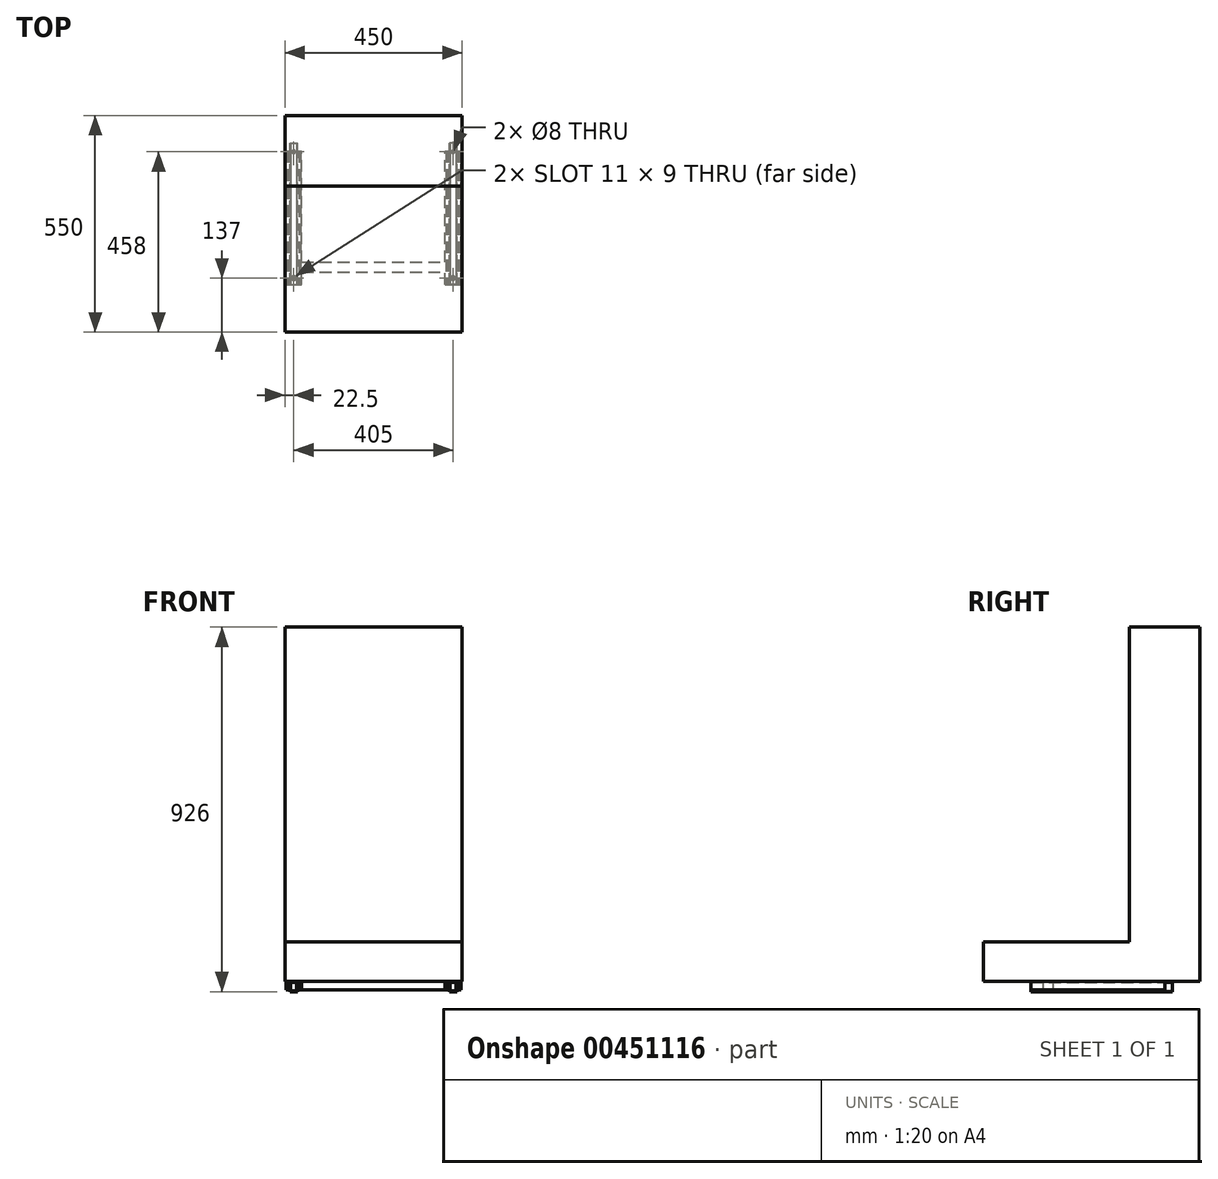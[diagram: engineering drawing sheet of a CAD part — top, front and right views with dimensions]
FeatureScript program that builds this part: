
annotation { "Feature Type Name" : "Feature", "Feature Type Description" : "" }
export const myFeature = defineFeature(function(context is Context, id is Id, definition is map)
    precondition{}
    {
        {
            var Q0;
            Q0=qCreatedBy(makeId("Right.planeOp"),FACE);
            var sketch = newSketch(context, id + "F0", { "sketchPlane" : qUnion([Q0])});
            skLineSegment(sketch, "E0.bottom", {"start": v(0, 0) * mm, "end": v(-550, 0) * mm});
            skLineSegment(sketch, "E0.top", {"start": v(0, 100) * mm, "end": v(-550, 100) * mm});
            skLineSegment(sketch, "E0.left", {"start": v(0, 0) * mm, "end": v(0, 100) * mm});
            skLineSegment(sketch, "E0.right", {"start": v(-550, 0) * mm, "end": v(-550, 100) * mm});
            skLineSegment(sketch, "E1.bottom", {"start": v(0, 100) * mm, "end": v(-179.87, 100) * mm});
            skLineSegment(sketch, "E1.top", {"start": v(0, 900) * mm, "end": v(-179.87, 900) * mm});
            skLineSegment(sketch, "E1.left", {"start": v(0, 100) * mm, "end": v(0, 900) * mm});
            skLineSegment(sketch, "E1.right", {"start": v(-179.87, 100) * mm, "end": v(-179.87, 900) * mm});
            skSolve(sketch);
        }
        {
            var Q0;
            Q0 = qSketchRegion(id + "F0", true);
            extrude(context, id + "F1", {"entities" : qUnion([Q0]), "depth" : 450 * mm, "offsetDistance" : 25 * mm});
        }
        {
            var Q0;
            Q0=makeQuery(id+"F1.opExtrude","SWEPT_FACE",FACE,{"disambiguationData":[OSD([sQuery(id+"F0.wireOp",EDGE,"E0.bottom")])]});
            var sketch = newSketch(context, id + "F2", { "sketchPlane" : qUnion([Q0])});
            skLineSegment(sketch, "E2.bottom", {"start": v(2.5, 430) * mm, "end": v(42.5, 430) * mm});
            skLineSegment(sketch, "E2.top", {"start": v(2.5, 90) * mm, "end": v(42.5, 90) * mm});
            skLineSegment(sketch, "E2.left", {"start": v(2.5, 430) * mm, "end": v(2.5, 90) * mm});
            skLineSegment(sketch, "E2.right", {"start": v(42.5, 430) * mm, "end": v(42.5, 90) * mm});
            skLineSegment(sketch, "E3.bottom", {"start": v(407.5, 430) * mm, "end": v(447.5, 430) * mm});
            skLineSegment(sketch, "E3.top", {"start": v(407.5, 90) * mm, "end": v(447.5, 90) * mm});
            skLineSegment(sketch, "E3.left", {"start": v(407.5, 430) * mm, "end": v(407.5, 90) * mm});
            skLineSegment(sketch, "E3.right", {"start": v(447.5, 430) * mm, "end": v(447.5, 90) * mm});
            skLineSegment(sketch, "E4.bottom", {"start": v(42.5, 397.78) * mm, "end": v(407.5, 397.78) * mm});
            skLineSegment(sketch, "E4.top", {"start": v(42.5, 372.84) * mm, "end": v(407.5, 372.84) * mm});
            skLineSegment(sketch, "E4.left", {"start": v(42.5, 397.78) * mm, "end": v(42.5, 372.84) * mm});
            skLineSegment(sketch, "E4.right", {"start": v(407.5, 397.78) * mm, "end": v(407.5, 372.84) * mm});
            skSolve(sketch);
        }
        {
            var Q0;
            Q0 = qSketchRegion(id + "F2", true);
            extrude(context, id + "F3", {"entities" : qUnion([Q0]), "depth" : 22 * mm, "offsetDistance" : 25 * mm});
        }
        {
            var Q0;
            Q0=makeQuery(id+"F3.opExtrude","SWEPT_FACE",FACE,{"disambiguationData":[OSD([sQuery(id+"F2.wireOp",EDGE,"E2.bottom")])]});
            var sketch = newSketch(context, id + "F4", { "sketchPlane" : qUnion([Q0])});
            skLineSegment(sketch, "E5.bottom", {"start": v(4.5, -2) * mm, "end": v(40.5, -2) * mm});
            skLineSegment(sketch, "E5.top", {"start": v(4.5, -20) * mm, "end": v(40.5, -20) * mm});
            skLineSegment(sketch, "E5.left", {"start": v(4.5, -2) * mm, "end": v(4.5, -20) * mm});
            skLineSegment(sketch, "E5.right", {"start": v(40.5, -2) * mm, "end": v(40.5, -20) * mm});
            skLineSegment(sketch, "E6.bottom", {"start": v(9.5, -20) * mm, "end": v(35.5, -20) * mm});
            skLineSegment(sketch, "E6.top", {"start": v(9.5, -22) * mm, "end": v(35.5, -22) * mm});
            skLineSegment(sketch, "E6.left", {"start": v(9.5, -20) * mm, "end": v(9.5, -22) * mm});
            skLineSegment(sketch, "E6.right", {"start": v(35.5, -20) * mm, "end": v(35.5, -22) * mm});
            skLineSegment(sketch, "E7.0", {"start": v(407.5, -22) * mm, "end": v(407.5, 0) * mm});
            skLineSegment(sketch, "E8.0", {"start": v(407.5, -22) * mm, "end": v(447.5, -22) * mm});
            skLineSegment(sketch, "E9.0", {"start": v(447.5, -22) * mm, "end": v(447.5, 0) * mm});
            skLineSegment(sketch, "E10.bottom", {"start": v(409.5, -2) * mm, "end": v(445.5, -2) * mm});
            skLineSegment(sketch, "E10.top", {"start": v(409.5, -20) * mm, "end": v(445.5, -20) * mm});
            skLineSegment(sketch, "E10.left", {"start": v(409.5, -2) * mm, "end": v(409.5, -20) * mm});
            skLineSegment(sketch, "E10.right", {"start": v(445.5, -2) * mm, "end": v(445.5, -20) * mm});
            skLineSegment(sketch, "E11.bottom", {"start": v(414.5, -20) * mm, "end": v(440.5, -20) * mm});
            skLineSegment(sketch, "E11.top", {"start": v(414.5, -22) * mm, "end": v(440.5, -22) * mm});
            skLineSegment(sketch, "E11.left", {"start": v(414.5, -20) * mm, "end": v(414.5, -22) * mm});
            skLineSegment(sketch, "E11.right", {"start": v(440.5, -20) * mm, "end": v(440.5, -22) * mm});
            skSolve(sketch);
        }
        {
            var Q0;
            Q0 = qSketchRegion(id + "F4", true);
            extrude(context, id + "F5", {"entities" : qUnion([Q0]), "operationType" : NewBodyOperationType.REMOVE, "oppositeDirection" : true, "depth" : 372 * mm, "offsetDistance" : 25 * mm});
        }
        {
            var Q0;
            Q0=makeQuery(id+"F5.boolean.opBoolean","COPY",FACE,{"derivedFrom":makeQuery(id+"F5.opExtrude","SWEPT_FACE",FACE,{"disambiguationData":[OSD([sQuery(id+"F4.wireOp",EDGE,"E5.bottom")])]})});
            var sketch = newSketch(context, id + "F6", { "sketchPlane" : qUnion([Q0])});
            skLineSegment(sketch, "E12.bottom", {"start": v(13, 430) * mm, "end": v(32, 430) * mm});
            skLineSegment(sketch, "E12.top", {"start": v(13, 70) * mm, "end": v(32, 70) * mm});
            skLineSegment(sketch, "E12.left", {"start": v(13, 430) * mm, "end": v(13, 70) * mm});
            skLineSegment(sketch, "E12.right", {"start": v(32, 430) * mm, "end": v(32, 70) * mm});
            skLineSegment(sketch, "E13", {"start": v(225, 523.36) * mm, "end": v(225, 219) * mm, "construction": true});
            skLineSegment(sketch, "E14.MirrorCS", {"start": v(437, 70) * mm, "end": v(418, 70) * mm});
            skLineSegment(sketch, "E15.MirrorCS", {"start": v(437, 430) * mm, "end": v(418, 430) * mm});
            skLineSegment(sketch, "E16.MirrorCS", {"start": v(418, 430) * mm, "end": v(418, 70) * mm});
            skLineSegment(sketch, "E17.MirrorCS", {"start": v(437, 430) * mm, "end": v(437, 70) * mm});
            skCircle(sketch, "E18", {"center": v(22.5, 92) * mm, "radius": 4 * mm});
            skPoint(sketch, "E18.centerSnap0", {"position": v(22.5, 70) * mm});
            skLineSegment(sketch, "E19.bottom", {"start": v(18, 415.68) * mm, "end": v(27, 415.68) * mm, "construction": true});
            skLineSegment(sketch, "E19.top", {"start": v(18, 410.32) * mm, "end": v(27, 410.32) * mm, "construction": true});
            skLineSegment(sketch, "E19.left", {"start": v(18, 415.68) * mm, "end": v(18, 410.32) * mm});
            skLineSegment(sketch, "E19.right", {"start": v(27, 415.68) * mm, "end": v(27, 410.32) * mm});
            skArc(sketch, "E20", {"start": v(27, 415.68) * mm, "mid": v(22.5, 418.5) * mm, "end": v(18, 415.68) * mm});
            skArc(sketch, "E21", {"start": v(18, 410.32) * mm, "mid": v(22.5, 407.5) * mm, "end": v(27, 410.32) * mm});
            skPoint(sketch, "E22", {"position": v(22.5, 430) * mm});
            skPoint(sketch, "E23", {"position": v(18, 413) * mm});
            skCircle(sketch, "E24.MirrorC", {"center": v(427.5, 92) * mm, "radius": 4 * mm});
            skLineSegment(sketch, "E25.MirrorCS", {"start": v(432, 415.68) * mm, "end": v(432, 410.32) * mm});
            skLineSegment(sketch, "E26.MirrorCS", {"start": v(423, 415.68) * mm, "end": v(423, 410.32) * mm});
            skPoint(sketch, "E27.MirrorP", {"position": v(432, 413) * mm});
            skLineSegment(sketch, "E28.MirrorCS", {"start": v(432, 415.68) * mm, "end": v(423, 415.68) * mm, "construction": true});
            skLineSegment(sketch, "E29.MirrorCS", {"start": v(432, 410.32) * mm, "end": v(423, 410.32) * mm, "construction": true});
            skArc(sketch, "E30.MirrorCS", {"start": v(423, 415.68) * mm, "mid": v(427.5, 418.5) * mm, "end": v(432, 415.68) * mm});
            skArc(sketch, "E31.MirrorCS", {"start": v(432, 410.32) * mm, "mid": v(427.5, 407.5) * mm, "end": v(423, 410.32) * mm});
            skSolve(sketch);
        }
        {
            var Q0;
            Q0 = qSketchRegion(id + "F6", true);
            extrude(context, id + "F7", {"entities" : qUnion([Q0]), "operationType" : NewBodyOperationType.ADD, "depth" : 24 * mm, "offsetDistance" : 25 * mm});
        }
        {
            var Q0;
            Q0=makeQuery(id+"F7.boolean.opBoolean","MERGE",FACE,{"derivedFrom":[makeQuery(id+"F3.opExtrude","SWEPT_FACE",FACE,{"disambiguationData":[OSD([sQuery(id+"F2.wireOp",EDGE,"E2.bottom")])]}),makeQuery(id+"F7.opExtrude","SWEPT_FACE",FACE,{"disambiguationData":[OSD([sQuery(id+"F6.wireOp",EDGE,"E12.bottom")])]})]});
            var sketch = newSketch(context, id + "F8", { "sketchPlane" : qUnion([Q0])});
            skLineSegment(sketch, "E32.bottom", {"start": v(15, -2) * mm, "end": v(30, -2) * mm});
            skLineSegment(sketch, "E32.top", {"start": v(15, -24) * mm, "end": v(30, -24) * mm});
            skLineSegment(sketch, "E32.left", {"start": v(15, -2) * mm, "end": v(15, -24) * mm});
            skLineSegment(sketch, "E32.right", {"start": v(30, -2) * mm, "end": v(30, -24) * mm});
            skLineSegment(sketch, "E33.bottom", {"start": v(420, -2) * mm, "end": v(435, -2) * mm});
            skLineSegment(sketch, "E33.top", {"start": v(420, -24) * mm, "end": v(435, -24) * mm});
            skLineSegment(sketch, "E33.left", {"start": v(420, -2) * mm, "end": v(420, -24) * mm});
            skLineSegment(sketch, "E33.right", {"start": v(435, -2) * mm, "end": v(435, -24) * mm});
            skSolve(sketch);
        }
        {
            var Q0;
            Q0 = qSketchRegion(id + "F8", true);
            extrude(context, id + "F9", {"entities" : qUnion([Q0]), "operationType" : NewBodyOperationType.REMOVE, "oppositeDirection" : true, "depth" : 420 * mm, "offsetDistance" : 25 * mm});
        }
    });
